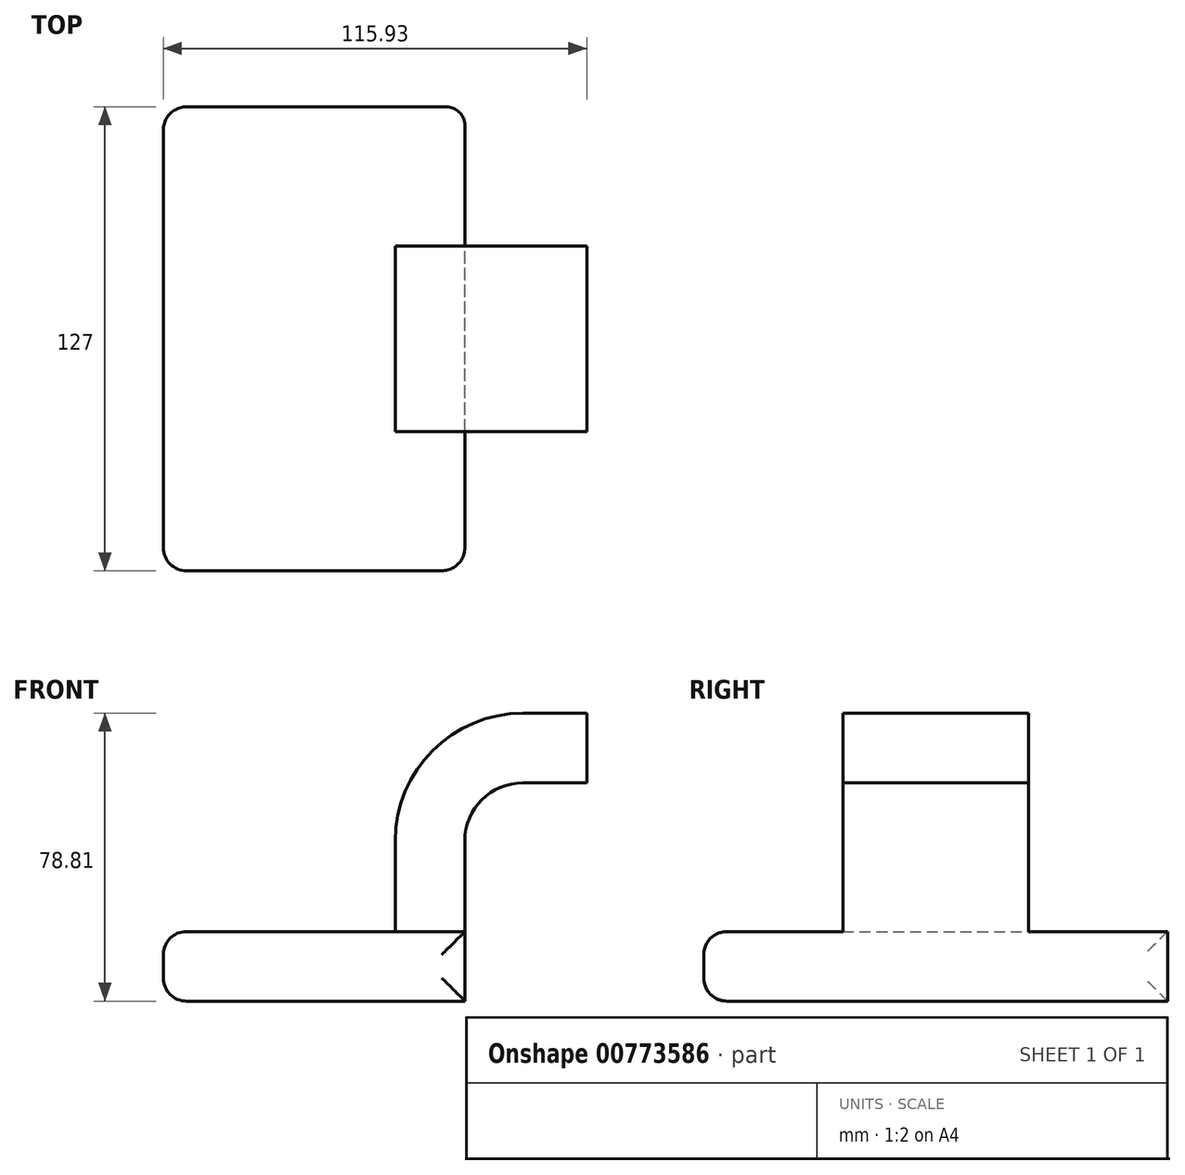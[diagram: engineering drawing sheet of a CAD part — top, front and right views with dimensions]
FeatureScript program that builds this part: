
annotation { "Feature Type Name" : "Feature", "Feature Type Description" : "" }
export const myFeature = defineFeature(function(context is Context, id is Id, definition is map)
    precondition{}
    {
        {
            var Q0;
            Q0=qCreatedBy(makeId("Front.planeOp"),FACE);
            var sketch = newSketch(context, id + "F0", { "sketchPlane" : qUnion([Q0])});
            skLineSegment(sketch, "E0.bottom", {"start": v(-41.28, 9.53) * mm, "end": v(41.28, 9.53) * mm});
            skLineSegment(sketch, "E0.top", {"start": v(-41.28, -9.53) * mm, "end": v(41.28, -9.53) * mm});
            skLineSegment(sketch, "E0.left", {"start": v(-41.28, 9.53) * mm, "end": v(-41.28, -9.53) * mm});
            skLineSegment(sketch, "E0.right", {"start": v(41.28, 9.53) * mm, "end": v(41.28, -9.53) * mm});
            skPoint(sketch, "E0.middle", {"position": v(0, 0) * mm});
            skLineSegment(sketch, "E1.bottom", {"start": v(72, 74.68) * mm, "end": v(122.8, 74.68) * mm});
            skLineSegment(sketch, "E1.top", {"start": v(72, 46.1) * mm, "end": v(122.8, 46.1) * mm});
            skLineSegment(sketch, "E1.left", {"start": v(72, 74.68) * mm, "end": v(72, 46.1) * mm});
            skLineSegment(sketch, "E1.right", {"start": v(122.8, 74.68) * mm, "end": v(122.8, 46.1) * mm});
            skLineSegment(sketch, "E2", {"start": v(41.28, 9.53) * mm, "end": v(41.27, 34.35) * mm});
            skArc(sketch, "E3", {"start": v(41.28, 34.35) * mm, "mid": v(45.92, 45.58) * mm, "end": v(57.15, 50.23) * mm});
            skLineSegment(sketch, "E4", {"start": v(57.15, 50.23) * mm, "end": v(74.66, 50.23) * mm});
            skLineSegment(sketch, "E5.0", {"start": v(57.15, 69.28) * mm, "end": v(74.66, 69.28) * mm});
            skArc(sketch, "E5.1", {"start": v(22.23, 34.35) * mm, "mid": v(32.45, 59.05) * mm, "end": v(57.15, 69.28) * mm});
            skLineSegment(sketch, "E5.2", {"start": v(22.23, 9.52) * mm, "end": v(22.23, 34.35) * mm});
            skLineSegment(sketch, "E6", {"start": v(74.66, 69.28) * mm, "end": v(74.66, 50.23) * mm});
            skFitSpline(sketch, "E7", {"points": [v(-41.28, 9.52) * mm, v(57.15, 69.28) * mm], "startDerivative": vector(148.17, 7.05) * mm, "endDerivative": vector(126.87, -4.37) * mm});
            skSolve(sketch);
        }
        {
            var Q0;
            Q0=makeQuery(id+"F0.imprint","IMPRINT",FACE,{"disambiguationData":[TD([[makeQuery(id+"F0.imprint","IMPRINT",EDGE,{"derivedFrom":sQuery(id+"F0.wireOp",EDGE,"E0.top")}),1.0]])]});
            extrude(context, id + "F1", {"entities" : qUnion([Q0]), "endBound" : BoundingType.SYMMETRIC, "depth" : 127 * mm, "offsetDistance" : 25.4 * mm});
        }
        {
            var Q0;
            {var subQ1=sQuery(id+"F0.wireOp",EDGE,"E2");Q0=makeQuery(id+"F0.imprint","IMPRINT",FACE,{"disambiguationData":[TD([[makeQuery(id+"F0.imprint","IMPRINT",EDGE,{"derivedFrom":subQ1}),1.0]])]});}
            var Q1;
            {var subQ5=sQuery(id+"F0.wireOp",EDGE,"E6");Q1=makeQuery(id+"F0.imprint","IMPRINT",FACE,{"disambiguationData":[TD([[makeQuery(id+"F0.imprint","IMPRINT",EDGE,{"derivedFrom":subQ5}),-1.0]])]});}
            extrude(context, id + "F2", {"entities" : qUnion([Q0, Q1]), "operationType" : NewBodyOperationType.ADD, "endBound" : BoundingType.SYMMETRIC, "depth" : 50.8 * mm, "offsetDistance" : 25.4 * mm});
        }
        {
            var Q0;
            Q0=makeQuery(id+"F0.imprint","IMPRINT",FACE,{"disambiguationData":[TD([[makeQuery(id+"F0.imprint","IMPRINT",EDGE,{"derivedFrom":sQuery(id+"F0.wireOp",EDGE,"E5.1")}),1.0]])]});
            extrude(context, id + "F3", {"entities" : qUnion([Q0]), "operationType" : NewBodyOperationType.ADD, "endBound" : BoundingType.SYMMETRIC, "depth" : 15.88 * mm, "offsetDistance" : 25.4 * mm});
        }
        {
            var Q0;
            Q0=makeQuery(id+"F1.opExtrude","SWEPT_FACE",FACE,{"disambiguationData":[OSD([sQuery(id+"F0.wireOp",EDGE,"E0.left")])]});
            var Q1;
            Q1=makeQuery(id+"F1.opExtrude","CAP_FACE",FACE,{"disambiguationData":[OSD([sQuery(id+"F0.wireOp",EDGE,"E0.bottom"),sQuery(id+"F0.wireOp",EDGE,"E0.top"),sQuery(id+"F0.wireOp",EDGE,"E0.left"),sQuery(id+"F0.wireOp",EDGE,"E0.right")])],"isStart":false});
            fillet(context, id + "F4", {"entities" : qUnion([Q0, Q1]), "radius" : 6.35 * mm, "tangentPropagation" : true, "allowEdgeOverflow" : false});
        }
        {
            var Q0;
            Q0=makeQuery(id+"F1.opExtrude","CAP_EDGE",EDGE,{"disambiguationData":[OSD([sQuery(id+"F0.wireOp",EDGE,"E0.left")])],"isStart":false});
            var Q1;
            Q1=makeQuery(id+"F1.opExtrude","CAP_EDGE",EDGE,{"disambiguationData":[OSD([sQuery(id+"F0.wireOp",EDGE,"E0.left")])],"isStart":true});
            var Q2;
            Q2=makeQuery(id+"F1.opExtrude","CAP_EDGE",EDGE,{"disambiguationData":[OSD([sQuery(id+"F0.wireOp",EDGE,"E0.right")])],"isStart":false});
            var Q3;
            Q3=makeQuery(id+"F1.opExtrude","CAP_EDGE",EDGE,{"disambiguationData":[OSD([sQuery(id+"F0.wireOp",EDGE,"E0.right")])],"isStart":true});
            fillet(context, id + "F5", {"entities" : qUnion([Q0, Q1, Q2, Q3]), "radius" : 5.08 * mm, "tangentPropagation" : true, "allowEdgeOverflow" : false});
        }
    });
